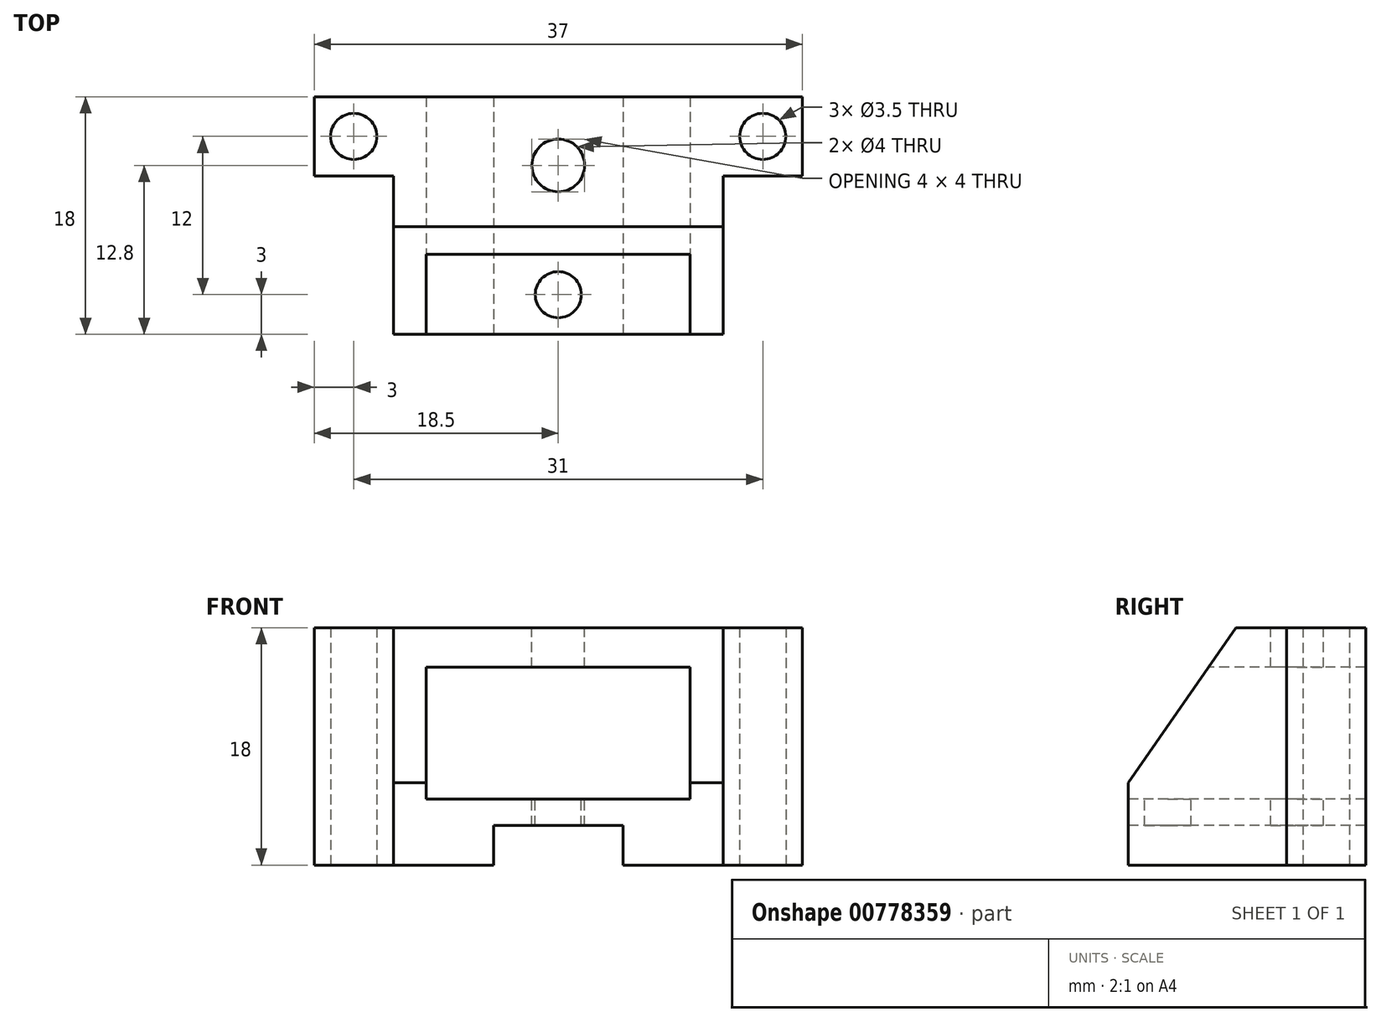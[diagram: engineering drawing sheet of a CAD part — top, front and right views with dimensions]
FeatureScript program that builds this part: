
annotation { "Feature Type Name" : "Feature", "Feature Type Description" : "" }
export const myFeature = defineFeature(function(context is Context, id is Id, definition is map)
    precondition{}
    {
        {
            var Q0;
            Q0=qCreatedBy(makeId("Top.planeOp"),FACE);
            var sketch = newSketch(context, id + "F0", { "sketchPlane" : qUnion([Q0])});
            skLineSegment(sketch, "E0.bottom", {"start": v(-12.5, 9) * mm, "end": v(12.5, 9) * mm});
            skLineSegment(sketch, "E0.top", {"start": v(-12.5, -9) * mm, "end": v(12.5, -9) * mm});
            skLineSegment(sketch, "E0.left", {"start": v(-12.5, 9) * mm, "end": v(-12.5, -9) * mm});
            skLineSegment(sketch, "E0.right", {"start": v(12.5, 9) * mm, "end": v(12.5, -9) * mm});
            skPoint(sketch, "E0.middle", {"position": v(0, 0) * mm});
            skLineSegment(sketch, "E1.bottom", {"start": v(-12.5, 9) * mm, "end": v(-18.5, 9) * mm});
            skLineSegment(sketch, "E1.top", {"start": v(-12.5, 3) * mm, "end": v(-18.5, 3) * mm});
            skLineSegment(sketch, "E1.left", {"start": v(-12.5, 9) * mm, "end": v(-12.5, 3) * mm});
            skLineSegment(sketch, "E1.right", {"start": v(-18.5, 9) * mm, "end": v(-18.5, 3) * mm});
            skLineSegment(sketch, "E2.MirrorCS", {"start": v(12.5, 3) * mm, "end": v(18.5, 3) * mm});
            skLineSegment(sketch, "E3.MirrorCS", {"start": v(18.5, 9) * mm, "end": v(18.5, 3) * mm});
            skLineSegment(sketch, "E4.MirrorCS", {"start": v(12.5, 9) * mm, "end": v(18.5, 9) * mm});
            skLineSegment(sketch, "E5", {"start": v(-15.5, 3) * mm, "end": v(-15.5, 6) * mm});
            skCircle(sketch, "E6", {"center": v(-15.5, 6) * mm, "radius": 1.75 * mm});
            skCircle(sketch, "E7.MirrorC", {"center": v(15.5, 6) * mm, "radius": 1.75 * mm});
            skSolve(sketch);
        }
        {
            var Q0;
            {var subQ1=sQuery(id+"F0.wireOp",EDGE,"E0.bottom");Q0=makeQuery(id+"F0.imprint","IMPRINT",FACE,{"disambiguationData":[TD([[makeQuery(id+"F0.imprint","IMPRINT",EDGE,{"derivedFrom":subQ1}),-1.0]])]});}
            var sketch = newSketch(context, id + "F1", { "sketchPlane" : qUnion([Q0])});
            skLineSegment(sketch, "E8.bottom", {"start": v(-4.9, 9) * mm, "end": v(4.9, 9) * mm});
            skLineSegment(sketch, "E8.top", {"start": v(-4.9, -9) * mm, "end": v(4.9, -9) * mm});
            skLineSegment(sketch, "E8.left", {"start": v(-4.9, 9) * mm, "end": v(-4.9, -9) * mm});
            skLineSegment(sketch, "E8.right", {"start": v(4.9, 9) * mm, "end": v(4.9, -9) * mm});
            skPoint(sketch, "E8.middle", {"position": v(0, 0) * mm});
            skSolve(sketch);
        }
        {
            var Q0;
            Q0 = qSketchRegion(id + "F0", true);
            extrude(context, id + "F2", {"entities" : qUnion([Q0]), "depth" : 18 * mm, "offsetDistance" : 25 * mm});
        }
        {
            var Q0;
            Q0=makeQuery(id+"F1.imprint","IMPRINT",FACE,{"disambiguationData":[TD([[makeQuery(id+"F1.imprint","IMPRINT",EDGE,{"derivedFrom":sQuery(id+"F1.wireOp",EDGE,"E8.bottom")}),-1.0]])]});
            extrude(context, id + "F3", {"entities" : qUnion([Q0]), "operationType" : NewBodyOperationType.REMOVE, "oppositeDirection" : true, "depth" : -3 * mm, "offsetDistance" : 25 * mm});
        }
        {
            var Q0;
            Q0=makeQuery(id+"F2.opExtrude","SWEPT_FACE",FACE,{"disambiguationData":[OSD([sQuery(id+"F0.wireOp",EDGE,"E0.top")])]});
            var sketch = newSketch(context, id + "F4", { "sketchPlane" : qUnion([Q0])});
            skLineSegment(sketch, "E9", {"start": v(0, 18) * mm, "end": v(0, 15) * mm});
            skLineSegment(sketch, "E10.bottom", {"start": v(0, 15) * mm, "end": v(10, 15) * mm});
            skLineSegment(sketch, "E10.top", {"start": v(0, 5) * mm, "end": v(10, 5) * mm});
            skLineSegment(sketch, "E10.left", {"start": v(0, 15) * mm, "end": v(0, 5) * mm});
            skLineSegment(sketch, "E10.right", {"start": v(10, 15) * mm, "end": v(10, 5) * mm});
            skLineSegment(sketch, "E11.MirrorCS", {"start": v(0, 15) * mm, "end": v(-10, 15) * mm});
            skLineSegment(sketch, "E12.MirrorCS", {"start": v(-10, 15) * mm, "end": v(-10, 5) * mm});
            skLineSegment(sketch, "E13.MirrorCS", {"start": v(0, 5) * mm, "end": v(-10, 5) * mm});
            skSolve(sketch);
        }
        {
            var Q0;
            Q0=makeQuery(id+"F4.imprint","IMPRINT",FACE,{"disambiguationData":[TD([[makeQuery(id+"F4.imprint","IMPRINT",EDGE,{"derivedFrom":sQuery(id+"F4.wireOp",EDGE,"E10.bottom")}),-1.0]])]});
            var Q1;
            Q1=makeQuery(id+"F4.imprint","IMPRINT",FACE,{"disambiguationData":[TD([[makeQuery(id+"F4.imprint","IMPRINT",EDGE,{"derivedFrom":sQuery(id+"F4.wireOp",EDGE,"E10.left")}),-1.0]])]});
            extrude(context, id + "F5", {"entities" : qUnion([Q0, Q1]), "operationType" : NewBodyOperationType.REMOVE, "oppositeDirection" : true, "depth" : 20 * mm, "offsetDistance" : 25 * mm});
        }
        {
            var Q0;
            Q0=makeQuery(id+"F2.opExtrude","CAP_FACE",FACE,{"disambiguationData":[OSD([sQuery(id+"F0.wireOp",EDGE,"E0.bottom"),sQuery(id+"F0.wireOp",EDGE,"E0.top"),sQuery(id+"F0.wireOp",EDGE,"E0.left"),sQuery(id+"F0.wireOp",EDGE,"E0.right"),sQuery(id+"F0.wireOp",EDGE,"E1.bottom"),sQuery(id+"F0.wireOp",EDGE,"E1.top"),sQuery(id+"F0.wireOp",EDGE,"E1.right"),sQuery(id+"F0.wireOp",EDGE,"E2.MirrorCS"),sQuery(id+"F0.wireOp",EDGE,"E3.MirrorCS"),sQuery(id+"F0.wireOp",EDGE,"E4.MirrorCS"),sQuery(id+"F0.wireOp",EDGE,"E6"),sQuery(id+"F0.wireOp",EDGE,"E7.MirrorC")])],"isStart":false});
            var sketch = newSketch(context, id + "F6", { "sketchPlane" : qUnion([Q0])});
            skLineSegment(sketch, "E14", {"start": v(0, -9) * mm, "end": v(0, -3) * mm});
            skLineSegment(sketch, "E15", {"start": v(0, -6) * mm, "end": v(0, 3.8) * mm});
            skCircle(sketch, "E16", {"center": v(0, -6) * mm, "radius": 1.75 * mm});
            skCircle(sketch, "E17", {"center": v(0, 3.8) * mm, "radius": 2 * mm});
            skSolve(sketch);
        }
        {
            var Q0;
            Q0=makeQuery(id+"F2.opExtrude","SWEPT_FACE",FACE,{"disambiguationData":[OSD([sQuery(id+"F0.wireOp",EDGE,"E0.left")])]});
            var sketch = newSketch(context, id + "F7", { "sketchPlane" : qUnion([Q0])});
            skLineSegment(sketch, "E18", {"start": v(9, 6.25) * mm, "end": v(0.85, 18) * mm});
            skSolve(sketch);
        }
        {
            var Q0;
            {var subQ0=sQuery(id+"F7.wireOp",EDGE,"E18");Q0=makeQuery(id+"F7.imprint","IMPRINT",FACE,{"disambiguationData":[TD([[makeQuery(id+"F7.imprint","IMPRINT",EDGE,{"derivedFrom":subQ0}),-1.0]])]});}
            extrude(context, id + "F8", {"entities" : qUnion([Q0]), "operationType" : NewBodyOperationType.REMOVE, "oppositeDirection" : true, "depth" : 25 * mm, "offsetDistance" : 25 * mm});
        }
        {
            var Q0;
            Q0=makeQuery(id+"F6.imprint","IMPRINT",FACE,{"disambiguationData":[TD([[makeQuery(id+"F6.imprint","IMPRINT",EDGE,{"derivedFrom":sQuery(id+"F6.wireOp",EDGE,"E17")}),1.0]])]});
            var Q1;
            {var subQ0=sQuery(id+"F6.wireOp",EDGE,"E15");var subQ1=sQuery(id+"F6.wireOp",EDGE,"E14");var subQ2=makeQuery(id+"F6.imprint","INTERSECT",VERTEX,{"derivedFrom":[subQ1,subQ0]});Q1=makeQuery(id+"F6.imprint","IMPRINT",FACE,{"disambiguationData":[TD([[makeQuery(id+"F6.imprint","IMPRINT",EDGE,{"disambiguationData":[TD([[subQ2,1.0]])],"derivedFrom":subQ1}),1.0]])]});}
            var Q2;
            {var subQ0=sQuery(id+"F6.wireOp",EDGE,"E15");var subQ1=sQuery(id+"F6.wireOp",EDGE,"E14");var subQ2=makeQuery(id+"F6.imprint","INTERSECT",VERTEX,{"derivedFrom":[subQ1,subQ0]});Q2=makeQuery(id+"F6.imprint","IMPRINT",FACE,{"disambiguationData":[TD([[makeQuery(id+"F6.imprint","IMPRINT",EDGE,{"disambiguationData":[TD([[subQ2,1.0]])],"derivedFrom":subQ1}),-1.0]])]});}
            extrude(context, id + "F9", {"entities" : qUnion([Q0, Q1, Q2]), "operationType" : NewBodyOperationType.REMOVE, "oppositeDirection" : true, "depth" : 25 * mm, "offsetDistance" : 25 * mm});
        }
    });
